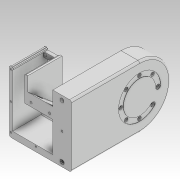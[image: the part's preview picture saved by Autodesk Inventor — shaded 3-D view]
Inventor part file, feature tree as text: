
AUTODESK INVENTOR PART (.ipt)
format: ipt  version: 2020 (Build 240168000, 168)  size: 1,399,808 bytes
history: native  units: mm
features: sketch x51, extrude x48, plane x9, projected_geometry x7, fillet x6, chamfer x3, revolve x3, pattern_circular x2, loft x1, mirror x1, other x1
ambient origin geometry x8: Origin, YZ Plane, XZ Plane, XY Plane, X Axis, Y Axis, Z Axis, Center Point
bodies: Solid1 (feature_tree)
feature tree (132):
  extrude  "Extrusion1"  Depth=250.0mm
  extrude  "Extrusion2"  Depth=100.0mm TaperAngle=0.0deg
  extrude  "Extrusion3"  TaperAngle=0.0deg  [1 undecoded]
  extrude  "Extrusion4"  Depth=10.0mm
  extrude  "Extrusion5"  Depth=30.0mm
  pattern_circular  "Circular Pattern1"  Count=8 Angle=360.0deg
  plane  "Work Plane1"
  plane  "Work Plane2"
  extrude  "Extrusion6"  Depth=30.0mm
  extrude  "Extrusion7"  Depth=10.0mm
  extrude  "Extrusion8"  Depth=10.0mm
  extrude  "Extrusion9"  [1 undecoded]
  chamfer  "Chamfer1"  Distance=10.0mm
  extrude  "Extrusion13"  Depth=10.0mm TaperAngle=0.0deg
  extrude  "Extrusion14"  Depth=3.0mm TaperAngle=0.0deg
  extrude  "Extrusion15"  Depth=3.0mm
  extrude  "Extrusion16"  Depth=3.0mm
  extrude  "Extrusion17"  Depth=80.5mm
  extrude  "Extrusion18"  Depth=60.0mm
  extrude  "Extrusion19"  Depth=80.0mm TaperAngle=360.0deg
  extrude  "Extrusion20"  Depth=15.5mm TaperAngle=0.0deg
  fillet  "Fillet2"  Radius=22.1mm
  pattern_circular  "Circular Pattern2"  Count=8 Angle=360.0deg
  extrude  "Extrusion21"  Depth=10.0mm
  extrude  "Extrusion22"  Depth=7.0mm
  plane  "Work Plane3"
  revolve  "Revolution1"  [1 undecoded]
  revolve  "Revolution2"  [1 undecoded]
  plane  "Work Plane4"
  extrude  "Extrusion23"  Depth=96.8mm TaperAngle=0.0deg
  extrude  "Extrusion24"  Depth=2.5mm
  fillet  "Fillet3"  Radius=5.2mm
  loft  "Loft1"
  extrude  "Extrusion25"  TaperAngle=90.0deg  [1 undecoded]
  extrude  "Extrusion26"  Depth=25.0mm
  extrude  "Extrusion27"  Depth=19.0mm
  extrude  "Extrusion28"  Depth=2.7mm
  plane  "Work Plane5"
  extrude  "Extrusion29"  Depth=5.5mm
  extrude  "Extrusion30"  TaperAngle=90.0deg  [1 undecoded]
  extrude  "Extrusion32"  Depth=18.8mm TaperAngle=0.0deg
  extrude  "Extrusion35"  Depth=6.0mm
  revolve  "Revolution3"  [1 undecoded]
  extrude  "Extrusion36"  [1 undecoded]
  plane  "Work Plane7"
  extrude  "Extrusion37"  Depth=1.0mm TaperAngle=0.0deg
  extrude  "Extrusion38"  Depth=5.0mm
  mirror  "Mirror1"
  extrude  "Extrusion39"  TaperAngle=0.0deg  [1 undecoded]
  extrude  "Extrusion40"  Depth=3.0mm
  extrude  "Extrusion41"  Depth=10.0mm
  chamfer  "Chamfer3"  [1 undecoded]
  fillet  "Fillet5"  [1 undecoded]
  extrude  "Extrusion42"  Depth=255.0mm TaperAngle=0.0deg
  extrude  "Extrusion43"  Depth=2.25mm
  plane  "Work Plane8"
  extrude  "Extrusion44"  Depth=52.0mm TaperAngle=0.0deg
  plane  "Work Plane9"
  extrude  "Extrusion45"  Depth=0.2mm
  extrude  "Extrusion46"  Depth=0.2mm
  fillet  "Fillet8"  Radius=3.0mm
  fillet  "Fillet6"  [1 undecoded]
  fillet  "Fillet7"  Radius=1.0mm
  sketch  "Sketch55"  dims[d137=1.0mm d138=0.0mm d139=-7.0mm]
  plane  "Work Plane10"
  extrude  "Extrusion48"  TaperAngle=90.0deg  [1 undecoded]
  extrude  "Extrusion49"  Depth=0.2mm
  extrude  "Extrusion50"  Depth=3.0mm
  extrude  "Extrusion51"  Depth=0.2mm TaperAngle=360.0deg
  extrude  "Extrusion52"  Depth=52.0mm TaperAngle=0.0deg
  chamfer  "Chamfer4"  Distance=8.0mm
  sketch  "Sketch62"  dims[d160=6.0mm d177=255.0mm d178=0.0mm]
  extrude  "Extrusion53"  Depth=0.2mm TaperAngle=0.0deg
  extrude  "Extrusion54"  Depth=0.2mm
  extrude  "Extrusion55"  Depth=0.2mm TaperAngle=0.0deg
  sketch  "Sketch1"  dims[d0=50.0mm d1=250.0mm]
  sketch  "Sketch2"  dims[d2=50.0mm d3=100.0mm d4=0.0mm]
  sketch  "Sketch4"  dims[d5=5.0mm d7=0.0mm d8=0.0mm]
  sketch  "Sketch5"  dims[d11=10.0mm d12=0.0mm d14=85.0mm]
  sketch  "Sketch7"  dims[d15=1.0mm d16=0.0mm d17=30.0mm]
  projected_geometry  "Projected Loop1"
  sketch  "Sketch8"  dims[d18=3.3mm]
  projected_geometry  "Projected Loop2"
  projected_geometry  "Projected Loop4"
  sketch  "Sketch9"  dims[d19=15.0mm d20=0.0mm d21=80.0mm d22=360.0deg]
  sketch  "Sketch10"  dims[d24=30.0mm d25=30.0mm]
  sketch  "Sketch14"  dims[d30=-5.0mm d31=10.0mm]
  sketch  "Sketch15"  dims[d32=10.0mm d33=10.0mm]
  sketch  "Sketch16"  dims[d34=31.5mm d35=0.0mm d36=-5.0mm d38=10.0mm d39=0.0mm]
  sketch  "Sketch17"  dims[d40=22.1mm d41=10.0mm d42=0.0mm]
  sketch  "Sketch18"  dims[d43=5.0mm d44=3.0mm d45=0.0mm]
  sketch  "Sketch19"  dims[d56=3.0mm d57=2.0mm d58=45.0deg d62=95.1mm]
  sketch  "Sketch20"  dims[d63=10.0mm d64=0.0mm d65=3.0mm]
  sketch  "Sketch21"  dims[d66=0.5mm d67=0.0mm d68=80.5mm]
  sketch  "Sketch22"  dims[d69=16.5mm d70=0.0mm d71=60.0mm]
  sketch  "Sketch23"  dims[d72=3.2mm d73=80.0mm d75=360.0deg]
  other  "Work Axis1"
  sketch  "Sketch24"  dims[d77=15.5mm d78=0.0mm d79=15.5mm d80=0.0mm d81=22.1mm]
  projected_geometry  "Projected Loop5"
  projected_geometry  "Projected Loop6"
  sketch  "Sketch26"  dims[d82=0.0mm d83=0.0mm]
  sketch  "Sketch27"  dims[d84=76.0mm]
  sketch  "Sketch28"  dims[d85=0.1mm d86=0.0mm]
  sketch  "Sketch29"  dims[d87=15.0mm]
  sketch  "Sketch30"  dims[d88=2.0mm]
  sketch  "Sketch31"  dims[d89=22.5mm]
  sketch  "Sketch32"  dims[d90=0.8mm d91=0.0mm]
  sketch  "Sketch33"  dims[d92=0.2mm d93=80.0mm d94=360.0deg]
  projected_geometry  "Projected Loop7"
  sketch  "Sketch34"  dims[d96=24.43461mm d97=10.0mm]
  sketch  "Sketch35"  dims[d98=6.25mm d99=7.0mm]
  sketch  "Sketch38"  dims[d100=6.25mm d101=7.0mm]
  sketch  "Sketch41"  dims[d102=5.0mm d103=0.0mm d104=25.0mm]
  sketch  "Sketch42"  dims[d105=16.1mm d106=96.8mm d107=0.0mm]
  sketch  "Sketch43"  dims[d108=0.0mm d109=2.5mm d110=5.2mm]
  sketch  "Sketch44"  dims[d111=1.0mm d112=5.0mm]
  sketch  "Sketch45"  dims[d113=5.2mm d114=90.0deg]
  sketch  "Sketch46"  dims[d115=15.0mm d116=25.0mm]
  sketch  "Sketch47"  dims[d117=25.0mm d118=19.0mm]
  projected_geometry  "Projected Loop8"
  sketch  "Sketch48"  dims[d119=19.0mm d120=2.7mm]
  sketch  "Sketch49"  dims[d122=4.0mm d123=0.0mm d124=5.5mm]
  sketch  "Sketch50"  dims[d125=2.0mm d126=0.0mm d127=90.0deg]
  sketch  "Sketch51"  dims[d128=2.0mm d129=18.8mm d130=0.0mm]
  sketch  "Sketch52"  dims[d131=111.25mm d132=0.0mm d133=6.0mm]
  sketch  "Sketch53"  dims[d134=4.0mm d135=0.0mm d136=1.0mm]
  sketch  "Sketch57"  dims[d140=1.0mm d141=1.0mm d142=0.0mm]
  sketch  "Sketch58"  dims[d143=7.0mm d144=5.0mm]
  sketch  "Sketch59"  dims[d145=6.0mm d146=0.0mm d147=90.0deg]
  sketch  "Sketch60"  dims[d148=0.0mm d149=90.0deg d150=3.0mm]
  sketch  "Sketch61"  dims[d151=10.0mm d152=0.0mm d155=110.0mm d156=0.0mm d157=0.0mm d159=30.0deg]
  sketch  "Sketch63"  dims[d179=5.0mm d180=2.25mm d181=52.0mm d182=0.0mm d183=16.1mm d184=1.0mm d185=3.0mm d186=30.0deg d187=1.0mm d188=90.0deg d189=60.0mm d190=3.0mm d191=80.0mm d193=360.0deg d195=52.0mm d196=0.0mm d197=8.0mm d198=0.5mm d199=0.0mm d200=6.0mm d201=1.2mm d202=0.0mm d203=15.0mm d204=20.0mm d205=10.0mm d206=0.0mm d207=1.0mm d208=22.0mm d209=2.0mm d210=0.0mm d211=0.0mm d212=2.0mm d213=2.0mm d214=0.0mm d215=2.0mm d216=2.0mm d217=45.0deg d218=3.0mm d219=5.0mm d220=2.0mm d221=0.0mm d223=30.0mm d224=3.5mm d225=32.0mm d226=0.0mm d227=-6.0mm d229=32.0mm d230=0.0mm d231=12.0mm d232=-17.0mm d233=2.0mm d234=3.0mm d235=30.0mm d237=30.0mm d238=10.0mm d240=10.0mm d242=10.0mm d243=11.0mm d244=0.0mm d245=7.0mm d246=102.5mm d247=0.0mm d248=3.0mm d249=1.0mm d250=3.0mm d254=55.0mm d255=0.0mm d256=0.0mm d257=11.0mm d258=1.5mm d259=1.5mm d260=1.8mm d261=0.0mm d262=5.0mm d263=8.0mm d264=2.0mm d265=3.0mm d266=3.0mm d267=5.55mm d268=0.0mm d269=2.5mm d270=50.0mm d271=0.0mm d272=10.0mm d273=8.0mm d274=3.5mm d276=4.0mm d277=4.0mm d278=5.0mm d279=4.0mm d280=0.0mm d281=4.0mm d282=2.0mm d283=45.0deg d284=7.0mm d285=0.15mm d286=10.0mm d287=0.0mm d288=10.0mm d289=0.0mm d290=0.2mm d291=0.0mm]
note: 13 required parameter values undecoded (feature->parameter linkage not recoverable at this tier; creation-order binding heuristic only, values carry confidence <= 0.55)